# Revit family: ASH_Contour21_S6362_BIM_GB
name_source: partatom
category: Plumbing Fixtures
revit_build: Autodesk Revit MEP 2012 (Build: 20110309_2315(x64)
units: mm (PartAtom-declared; Revit-internal decimal feet)

## types (2) — shared parameters
AccessibilityPerformance = DDA Compliant
Accessories = www.idealspec.co.uk
Assembly Code = C1030200
AssetType = Fixed
BIMObjectName = GRABRAIL_ArmitageShanks_Contour21-ContemporaryHinged80cm_S6362
BREEAM Approved = No
Brand = Armitage Shanks
Category = Furntiure_GRABRAIL_UK
ConnectionType = Mechanical
CurrentRevision = 1
Default Elevation = 680 mm  [stored 2.23097 ft]
Description = Contour 21 hinged Contemporarty support rail 80cm, Doc M Compliant
DurationUnit = Years
ECA = No
ElementType = GRAB RAIL: Safety device to aid maintaining balance, lessen fatigue and assist in supporting weight whilst maneuvering the body
ExpectedLife = 30
Features = hinged support rail 80cm, Doc M Compliant Stainless Steel
Help = http://www.idealspec.co.uk
InstallationInstructions = http://www.idealspec.co.uk
Manufacturer = Ideal Standard International Ltd
ManufacturerURL = www.idealspec.co.uk
Material = Aluminium
NBSReference = 436
Name = GRABRAIL_ArmitageShanks_Contour21-ContemporaryHinged80cm_S6362
NettWeight = 3.15Kg
NominalHeight = 201 mm
NominalLength = 800 mm  [stored 2.62467 ft]
NominalWidth = 107 mm  [stored 0.35105 ft]
PredefinedType = grabrail
ProductDataSheet = http://www.idealspec.co.uk
ProductInformation = http://www.idealspec.co.uk
SalesInformation = http://www.idealspec.co.uk
SendEnquiry = http://www.idealspec.co.uk
Shape = Tubular
Size = mm x mm x mm
Space = Internal
SpareParts = www.fastpart-spares.co.uk
StandardsConformance = DDA, Doc-M
TRHColour = GRABRAIL_ArmitageShanks_Contour21-TRHolder-S6363AC : S6363LJ
URL = www.idealspec.co.uk
Version = 1
VolumeUnits = Litres
WRAS = No
WarrantyDescription = Manufacturers Warranty
WarrantyDurationParts = 5
WarrantyDurationUnit = Years
WarrantyGuarantorParts = Ideal Standard International Ltd
WaterEfficientProduct = No

## per-type parameters (varying)
| type | BarCode | Colour | Finish |
| S6362MY | 5017830445005 | Stainless Steel MY | Stainless Steel MY |
| S6362AA | 5017830444992 | Chrome | Chrome |

note: column(s) folded — value = type name in every type: Model, ModelNumber, ModelReference, PartNumber

note: [stored X ft] marks values corroborated as IEEE doubles in the binary element streams (Revit-internal decimal feet)

## geometry (parser evidence)
native form markers: Blend x8, Sweep x3
no freeform markers — native parametric forms only
